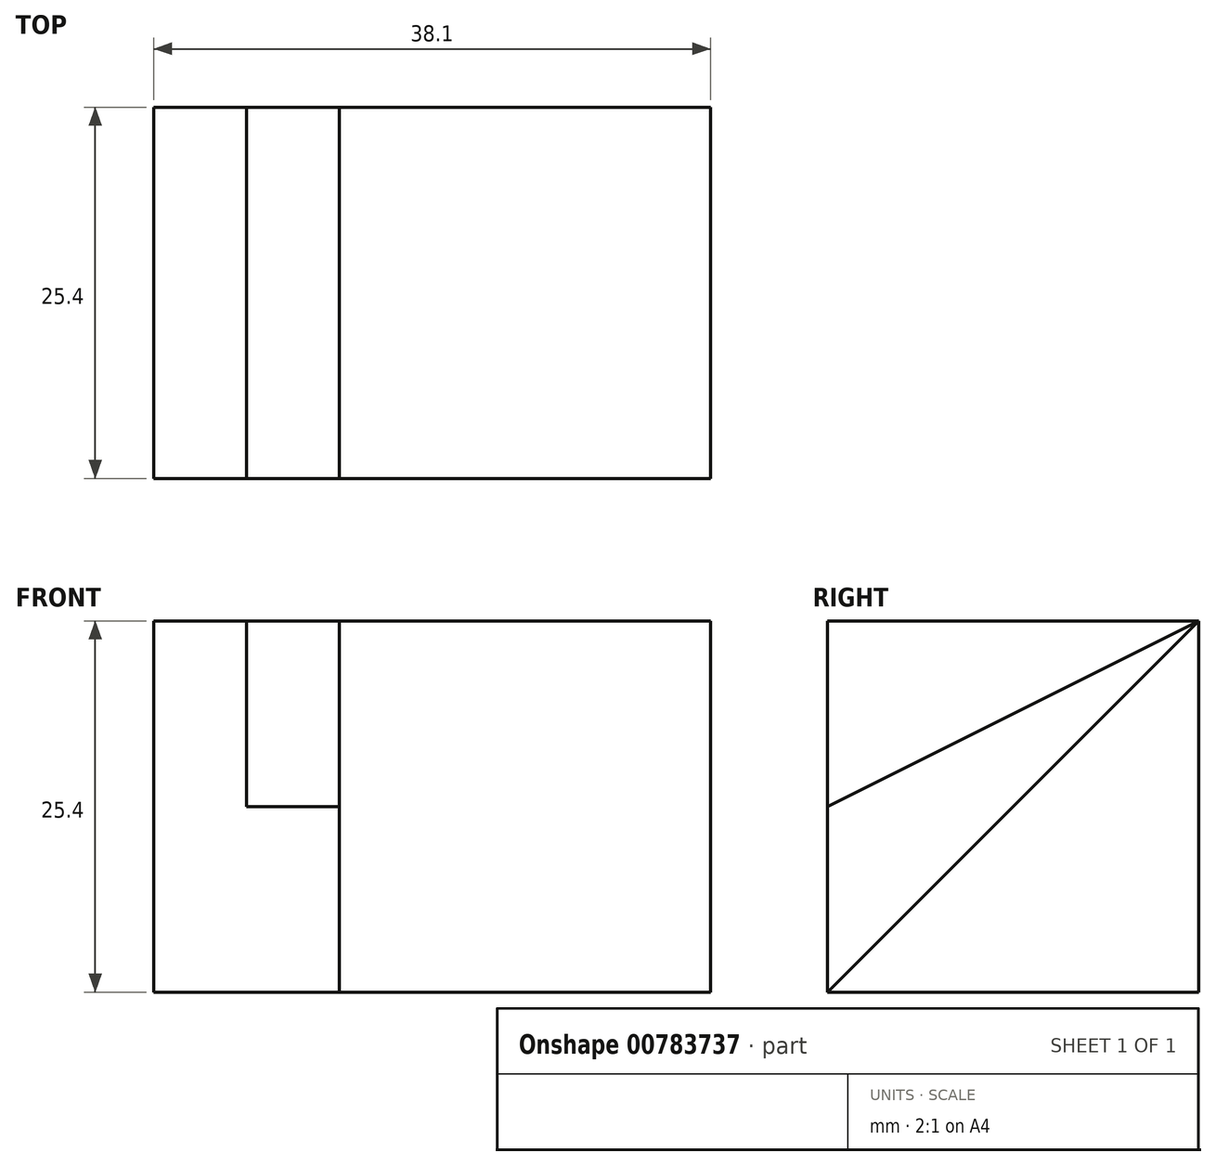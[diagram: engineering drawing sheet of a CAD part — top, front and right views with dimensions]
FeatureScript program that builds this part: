
annotation { "Feature Type Name" : "Feature", "Feature Type Description" : "" }
export const myFeature = defineFeature(function(context is Context, id is Id, definition is map)
    precondition{}
    {
        {
            var Q0;
            Q0=qCreatedBy(makeId("Front.planeOp"),FACE);
            var sketch = newSketch(context, id + "F0", { "sketchPlane" : qUnion([Q0])});
            skLineSegment(sketch, "E0", {"start": v(2.38, 0) * mm, "end": v(40.48, 0) * mm});
            skLineSegment(sketch, "E1", {"start": v(40.48, 0) * mm, "end": v(40.48, 25.4) * mm});
            skLineSegment(sketch, "E2", {"start": v(40.48, 25.4) * mm, "end": v(2.38, 25.4) * mm});
            skLineSegment(sketch, "E3", {"start": v(2.38, 0) * mm, "end": v(2.38, 25.4) * mm});
            skSolve(sketch);
        }
        {
            var Q0;
            Q0 = qSketchRegion(id + "F0", true);
            extrude(context, id + "F1", {"entities" : qUnion([Q0]), "depth" : 25.4 * mm, "offsetDistance" : 25.4 * mm});
        }
        {
            var Q0;
            Q0=makeQuery(id+"F1.opExtrude","SWEPT_FACE",FACE,{"disambiguationData":[OSD([sQuery(id+"F0.wireOp",EDGE,"E1")])]});
            var sketch = newSketch(context, id + "F2", { "sketchPlane" : qUnion([Q0])});
            skLineSegment(sketch, "E4", {"start": v(0, 25.4) * mm, "end": v(-25.4, 0) * mm});
            skSolve(sketch);
        }
        {
            var Q0;
            Q0 = qSketchRegion(id + "F2", true);
            var Q1;
            Q1=makeQuery(id+"F2.imprint","IMPRINT",FACE,{"disambiguationData":[TD([[makeQuery(id+"F2.imprint","IMPRINT",EDGE,{"derivedFrom":sQuery(id+"F2.wireOp",EDGE,"E4")}),-1.0]])]});
            extrude(context, id + "F3", {"entities" : qUnion([Q0, Q1]), "operationType" : NewBodyOperationType.REMOVE, "oppositeDirection" : true, "depth" : 25.4 * mm, "offsetDistance" : 25.4 * mm});
        }
        {
            var Q0;
            Q0=makeQuery(id+"F3.boolean.opBoolean","COPY",FACE,{"derivedFrom":makeQuery(id+"F3.opExtrude","CAP_FACE",FACE,{"disambiguationData":[OSD([sQuery(id+"F0.wireOp",EDGE,"E1"),sQuery(id+"F0.wireOp",EDGE,"E2"),sQuery(id+"F2.wireOp",EDGE,"E4")])],"isStart":false})});
            var sketch = newSketch(context, id + "F4", { "sketchPlane" : qUnion([Q0])});
            skLineSegment(sketch, "E5", {"start": v(-25.4, 0) * mm, "end": v(-25.4, 12.7) * mm});
            skLineSegment(sketch, "E6", {"start": v(-25.4, 12.7) * mm, "end": v(0, 25.4) * mm});
            skSolve(sketch);
        }
        {
            var Q0;
            {var subQ0=sQuery(id+"F4.wireOp",EDGE,"E6");Q0=makeQuery(id+"F4.imprint","IMPRINT",FACE,{"disambiguationData":[TD([[makeQuery(id+"F4.imprint","IMPRINT",EDGE,{"derivedFrom":subQ0}),1.0]])]});}
            extrude(context, id + "F5", {"entities" : qUnion([Q0]), "operationType" : NewBodyOperationType.REMOVE, "oppositeDirection" : true, "depth" : 6.35 * mm, "offsetDistance" : 25.4 * mm});
        }
    });
